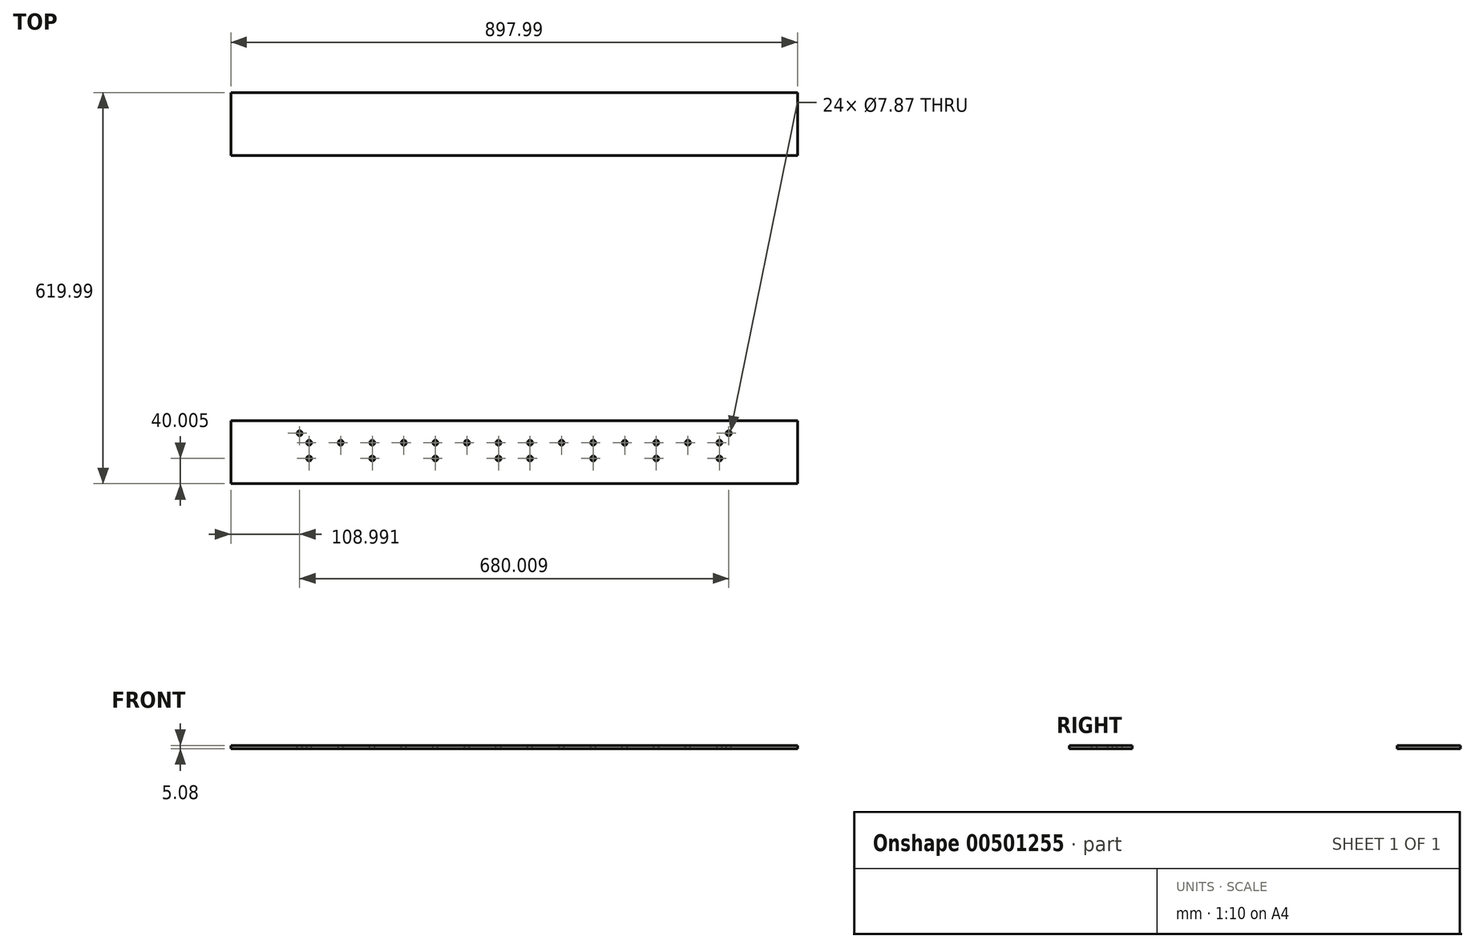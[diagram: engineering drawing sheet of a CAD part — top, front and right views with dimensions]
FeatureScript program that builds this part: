
annotation { "Feature Type Name" : "Feature", "Feature Type Description" : "" }
export const myFeature = defineFeature(function(context is Context, id is Id, definition is map)
    precondition{}
    {
        {
            var Q0;
            Q0=qCreatedBy(makeId("Top.planeOp"),FACE);
            var sketch = newSketch(context, id + "F0", { "sketchPlane" : qUnion([Q0])});
            skLineSegment(sketch, "E0.bottom", {"start": v(0, 0) * mm, "end": v(898, 0) * mm});
            skLineSegment(sketch, "E0.top", {"start": v(0, 100) * mm, "end": v(898, 100) * mm});
            skLineSegment(sketch, "E0.left", {"start": v(0, 0) * mm, "end": v(0, 100) * mm});
            skLineSegment(sketch, "E0.right", {"start": v(898, 0) * mm, "end": v(898, 100) * mm});
            skLineSegment(sketch, "E1.bottom", {"start": v(0, 100) * mm, "end": v(138.99, 100) * mm});
            skLineSegment(sketch, "E1.top", {"start": v(0, 519.99) * mm, "end": v(138.99, 519.99) * mm});
            skLineSegment(sketch, "E1.left", {"start": v(0, 100) * mm, "end": v(0, 519.99) * mm});
            skLineSegment(sketch, "E1.right", {"start": v(138.99, 100) * mm, "end": v(138.99, 519.99) * mm});
            skLineSegment(sketch, "E2.MirrorCS", {"start": v(898, 100) * mm, "end": v(759, 100) * mm});
            skLineSegment(sketch, "E3.MirrorCS", {"start": v(898, 100) * mm, "end": v(898, 519.99) * mm});
            skLineSegment(sketch, "E4.MirrorCS", {"start": v(898, 519.99) * mm, "end": v(759, 519.99) * mm});
            skLineSegment(sketch, "E5.MirrorCS", {"start": v(759, 100) * mm, "end": v(759, 519.99) * mm});
            skLineSegment(sketch, "E6.MirrorCS", {"start": v(0, 519.99) * mm, "end": v(898, 519.99) * mm});
            skLineSegment(sketch, "E7.MirrorCS", {"start": v(0, 619.99) * mm, "end": v(0, 519.99) * mm});
            skLineSegment(sketch, "E8.MirrorCS", {"start": v(0, 619.99) * mm, "end": v(898, 619.99) * mm});
            skLineSegment(sketch, "E9.MirrorCS", {"start": v(898, 619.99) * mm, "end": v(898, 519.99) * mm});
            skSolve(sketch);
        }
        {
            var Q0;
            Q0=makeQuery(id+"F0.imprint","IMPRINT",FACE,{"disambiguationData":[TD([[makeQuery(id+"F0.imprint","IMPRINT",EDGE,{"derivedFrom":sQuery(id+"F0.wireOp",EDGE,"E1.bottom")}),1.0]])]});
            var Q1;
            {var subQ0=sQuery(id+"F0.wireOp",EDGE,"E7.MirrorCS");Q1=makeQuery(id+"F0.imprint","IMPRINT",FACE,{"disambiguationData":[TD([[makeQuery(id+"F0.imprint","IMPRINT",EDGE,{"derivedFrom":subQ0}),1.0]])]});}
            var Q2;
            Q2=makeQuery(id+"F0.imprint","IMPRINT",FACE,{"disambiguationData":[TD([[makeQuery(id+"F0.imprint","IMPRINT",EDGE,{"derivedFrom":sQuery(id+"F0.wireOp",EDGE,"E2.MirrorCS")}),-1.0]])]});
            var Q3;
            Q3=makeQuery(id+"F0.imprint","IMPRINT",FACE,{"disambiguationData":[TD([[makeQuery(id+"F0.imprint","IMPRINT",EDGE,{"derivedFrom":sQuery(id+"F0.wireOp",EDGE,"E0.bottom")}),1.0]])]});
            extrude(context, id + "F1", {"entities" : qUnion([Q0, Q1, Q2, Q3]), "depth" : 5.08 * mm, "offsetDistance" : 25.4 * mm});
        }
        {
            var Q0;
            Q0=makeQuery(id+"F1.opExtrude","CAP_FACE",FACE,{"disambiguationData":[OSD([sQuery(id+"F0.wireOp",EDGE,"E0.bottom"),sQuery(id+"F0.wireOp",EDGE,"E0.top"),sQuery(id+"F0.wireOp",EDGE,"E0.left"),sQuery(id+"F0.wireOp",EDGE,"E0.right"),sQuery(id+"F0.wireOp",EDGE,"E1.left"),sQuery(id+"F0.wireOp",EDGE,"E1.right"),sQuery(id+"F0.wireOp",EDGE,"E3.MirrorCS"),sQuery(id+"F0.wireOp",EDGE,"E5.MirrorCS"),sQuery(id+"F0.wireOp",EDGE,"E6.MirrorCS"),sQuery(id+"F0.wireOp",EDGE,"E7.MirrorCS"),sQuery(id+"F0.wireOp",EDGE,"E8.MirrorCS"),sQuery(id+"F0.wireOp",EDGE,"E9.MirrorCS")])],"isStart":false});
            var sketch = newSketch(context, id + "F2", { "sketchPlane" : qUnion([Q0])});
            skLineSegment(sketch, "E10", {"start": v(0, 0) * mm, "end": v(124, 0) * mm});
            skLineSegment(sketch, "E11", {"start": v(124, 0) * mm, "end": v(124, 40) * mm});
            skLineSegment(sketch, "E12", {"start": v(124, 40) * mm, "end": v(124, 65) * mm});
            skCircle(sketch, "E13", {"center": v(124, 65) * mm, "radius": 3.94 * mm});
            skCircle(sketch, "E14.1.0.0", {"center": v(174.02, 65) * mm, "radius": 3.94 * mm});
            skCircle(sketch, "E14.2.0.0", {"center": v(224.03, 65) * mm, "radius": 3.94 * mm});
            skCircle(sketch, "E14.3.0.0", {"center": v(274.04, 65) * mm, "radius": 3.94 * mm});
            skCircle(sketch, "E14.4.0.0", {"center": v(324.05, 65) * mm, "radius": 3.94 * mm});
            skCircle(sketch, "E14.5.0.0", {"center": v(374.07, 65) * mm, "radius": 3.94 * mm});
            skCircle(sketch, "E14.6.0.0", {"center": v(424.08, 65) * mm, "radius": 3.94 * mm});
            skCircle(sketch, "E14.7.0.0", {"center": v(474.1, 65) * mm, "radius": 3.94 * mm});
            skCircle(sketch, "E14.8.0.0", {"center": v(524.1, 65) * mm, "radius": 3.94 * mm});
            skCircle(sketch, "E14.9.0.0", {"center": v(574.12, 65) * mm, "radius": 3.94 * mm});
            skCircle(sketch, "E14.10.0.0", {"center": v(624.13, 65) * mm, "radius": 3.94 * mm});
            skCircle(sketch, "E14.11.0.0", {"center": v(674.14, 65) * mm, "radius": 3.94 * mm});
            skCircle(sketch, "E14.12.0.0", {"center": v(724.15, 65) * mm, "radius": 3.94 * mm});
            skCircle(sketch, "E14.13.0.0", {"center": v(774.17, 65) * mm, "radius": 3.94 * mm});
            skLineSegment(sketch, "E14.direction1", {"start": v(124, 65) * mm, "end": v(174.02, 65) * mm, "construction": true});
            skLineSegment(sketch, "E15", {"start": v(138.99, 310) * mm, "end": v(268.02, 310) * mm});
            skPoint(sketch, "E15.endSnap0", {"position": v(138.99, 310) * mm});
            skCircle(sketch, "E16", {"center": v(124, 40) * mm, "radius": 3.94 * mm});
            skCircle(sketch, "E17.1.0.0", {"center": v(224.03, 40) * mm, "radius": 3.94 * mm});
            skCircle(sketch, "E17.2.0.0", {"center": v(324.05, 40) * mm, "radius": 3.94 * mm});
            skCircle(sketch, "E17.3.0.0", {"center": v(424.08, 40) * mm, "radius": 3.94 * mm});
            skLineSegment(sketch, "E17.direction1", {"start": v(124, 40) * mm, "end": v(224.03, 40) * mm, "construction": true});
            skLineSegment(sketch, "E18", {"start": v(424.08, 40) * mm, "end": v(474.1, 40) * mm});
            skCircle(sketch, "E19", {"center": v(474.1, 40) * mm, "radius": 3.94 * mm});
            skCircle(sketch, "E20.1.0.0", {"center": v(574.12, 40) * mm, "radius": 3.94 * mm});
            skCircle(sketch, "E20.2.0.0", {"center": v(674.14, 40) * mm, "radius": 3.94 * mm});
            skCircle(sketch, "E20.3.0.0", {"center": v(774.17, 40) * mm, "radius": 3.94 * mm});
            skLineSegment(sketch, "E20.direction1", {"start": v(474.1, 40) * mm, "end": v(574.12, 40) * mm, "construction": true});
            skCircle(sketch, "E21.MirrorC", {"center": v(124, 579.98) * mm, "radius": 3.94 * mm});
            skCircle(sketch, "E22.MirrorC", {"center": v(124, 555) * mm, "radius": 3.94 * mm});
            skCircle(sketch, "E23.MirrorC", {"center": v(174.02, 555) * mm, "radius": 3.94 * mm});
            skCircle(sketch, "E24.MirrorC", {"center": v(224.03, 555) * mm, "radius": 3.94 * mm});
            skCircle(sketch, "E25.MirrorC", {"center": v(224.03, 579.98) * mm, "radius": 3.94 * mm});
            skCircle(sketch, "E26.MirrorC", {"center": v(274.04, 555) * mm, "radius": 3.94 * mm});
            skCircle(sketch, "E27.MirrorC", {"center": v(324.05, 555) * mm, "radius": 3.94 * mm});
            skCircle(sketch, "E28.MirrorC", {"center": v(324.05, 579.98) * mm, "radius": 3.94 * mm});
            skCircle(sketch, "E29.MirrorC", {"center": v(374.07, 555) * mm, "radius": 3.94 * mm});
            skCircle(sketch, "E30.MirrorC", {"center": v(424.08, 555) * mm, "radius": 3.94 * mm});
            skCircle(sketch, "E31.MirrorC", {"center": v(424.08, 579.98) * mm, "radius": 3.94 * mm});
            skCircle(sketch, "E32.MirrorC", {"center": v(474.1, 555) * mm, "radius": 3.94 * mm});
            skCircle(sketch, "E33.MirrorC", {"center": v(474.1, 579.98) * mm, "radius": 3.94 * mm});
            skCircle(sketch, "E34.MirrorC", {"center": v(524.1, 555) * mm, "radius": 3.94 * mm});
            skCircle(sketch, "E35.MirrorC", {"center": v(624.13, 555) * mm, "radius": 3.94 * mm});
            skCircle(sketch, "E36.MirrorC", {"center": v(674.14, 555) * mm, "radius": 3.94 * mm});
            skCircle(sketch, "E37.MirrorC", {"center": v(674.14, 579.98) * mm, "radius": 3.94 * mm});
            skCircle(sketch, "E38.MirrorC", {"center": v(724.15, 555) * mm, "radius": 3.94 * mm});
            skCircle(sketch, "E39.MirrorC", {"center": v(774.17, 555) * mm, "radius": 3.94 * mm});
            skCircle(sketch, "E40.MirrorC", {"center": v(774.17, 579.98) * mm, "radius": 3.94 * mm});
            skCircle(sketch, "E41.MirrorC", {"center": v(574.12, 555) * mm, "radius": 3.94 * mm});
            skCircle(sketch, "E42.MirrorC", {"center": v(574.12, 579.98) * mm, "radius": 3.94 * mm});
            skLineSegment(sketch, "E43", {"start": v(124, 65) * mm, "end": v(109, 65) * mm});
            skLineSegment(sketch, "E44", {"start": v(109, 65) * mm, "end": v(109, 80) * mm});
            skCircle(sketch, "E45", {"center": v(109, 80) * mm, "radius": 3.94 * mm});
            skLineSegment(sketch, "E46", {"start": v(449, 100) * mm, "end": v(449, 150.02) * mm});
            skCircle(sketch, "E47.MirrorC", {"center": v(789, 80) * mm, "radius": 3.94 * mm});
            skCircle(sketch, "E48.MirrorC", {"center": v(109, 539.98) * mm, "radius": 3.94 * mm});
            skCircle(sketch, "E49.MirrorC", {"center": v(789, 539.98) * mm, "radius": 3.94 * mm});
            skCircle(sketch, "E50.0.1.0", {"center": v(109, 130.02) * mm, "radius": 3.94 * mm});
            skCircle(sketch, "E50.0.2.0", {"center": v(109, 180.04) * mm, "radius": 3.94 * mm});
            skCircle(sketch, "E50.0.3.0", {"center": v(109, 230.05) * mm, "radius": 3.94 * mm});
            skCircle(sketch, "E50.0.4.0", {"center": v(109, 280.06) * mm, "radius": 3.94 * mm});
            skCircle(sketch, "E50.0.5.0", {"center": v(109, 330.07) * mm, "radius": 3.94 * mm});
            skCircle(sketch, "E50.0.6.0", {"center": v(109, 380.09) * mm, "radius": 3.94 * mm});
            skCircle(sketch, "E50.0.7.0", {"center": v(109, 430.1) * mm, "radius": 3.94 * mm});
            skCircle(sketch, "E50.0.8.0", {"center": v(109, 480.11) * mm, "radius": 3.94 * mm});
            skLineSegment(sketch, "E50.direction1", {"start": v(109, 80) * mm, "end": v(134.4, 80) * mm, "construction": true});
            skLineSegment(sketch, "E50.direction2", {"start": v(109, 80) * mm, "end": v(109, 130.02) * mm, "construction": true});
            skLineSegment(sketch, "E51", {"start": v(109, 130.02) * mm, "end": v(84, 130.02) * mm});
            skLineSegment(sketch, "E52", {"start": v(84, 130.02) * mm, "end": v(84, 145.03) * mm});
            skCircle(sketch, "E53", {"center": v(84, 145.03) * mm, "radius": 3.94 * mm});
            skCircle(sketch, "E54.0.1.0", {"center": v(84, 225.04) * mm, "radius": 3.94 * mm});
            skCircle(sketch, "E54.0.2.0", {"center": v(84, 305.05) * mm, "radius": 3.94 * mm});
            skCircle(sketch, "E54.0.3.0", {"center": v(84, 385.06) * mm, "radius": 3.94 * mm});
            skCircle(sketch, "E54.0.4.0", {"center": v(84, 465.07) * mm, "radius": 3.94 * mm});
            skLineSegment(sketch, "E54.direction1", {"start": v(84, 145.03) * mm, "end": v(109.4, 145.03) * mm, "construction": true});
            skLineSegment(sketch, "E54.direction2", {"start": v(84, 145.03) * mm, "end": v(84, 225.04) * mm, "construction": true});
            skCircle(sketch, "E55.MirrorC", {"center": v(789, 480.11) * mm, "radius": 3.94 * mm});
            skCircle(sketch, "E56.MirrorC", {"center": v(814, 465.07) * mm, "radius": 3.94 * mm});
            skCircle(sketch, "E57.MirrorC", {"center": v(789, 430.1) * mm, "radius": 3.94 * mm});
            skCircle(sketch, "E58.MirrorC", {"center": v(814, 385.06) * mm, "radius": 3.94 * mm});
            skCircle(sketch, "E59.MirrorC", {"center": v(789, 380.09) * mm, "radius": 3.94 * mm});
            skCircle(sketch, "E60.MirrorC", {"center": v(789, 330.07) * mm, "radius": 3.94 * mm});
            skCircle(sketch, "E61.MirrorC", {"center": v(814, 305.05) * mm, "radius": 3.94 * mm});
            skCircle(sketch, "E62.MirrorC", {"center": v(789, 280.06) * mm, "radius": 3.94 * mm});
            skCircle(sketch, "E63.MirrorC", {"center": v(789, 130.02) * mm, "radius": 3.94 * mm});
            skCircle(sketch, "E64.MirrorC", {"center": v(814, 145.03) * mm, "radius": 3.94 * mm});
            skCircle(sketch, "E65.MirrorC", {"center": v(789, 180.04) * mm, "radius": 3.94 * mm});
            skCircle(sketch, "E66.MirrorC", {"center": v(814, 225.04) * mm, "radius": 3.94 * mm});
            skCircle(sketch, "E67.MirrorC", {"center": v(789, 230.05) * mm, "radius": 3.94 * mm});
            skSolve(sketch);
        }
        {
            var Q0;
            Q0=sQuery(id+"F2.wireOp",VERTEX,"E48.MirrorC.center");
            var Q1;
            Q1=sQuery(id+"F2.wireOp",VERTEX,"E22.MirrorC.center");
            var Q2;
            Q2=sQuery(id+"F2.wireOp",VERTEX,"E23.MirrorC.center");
            var Q3;
            Q3=sQuery(id+"F2.wireOp",VERTEX,"E21.MirrorC.center");
            var Q4;
            Q4=sQuery(id+"F2.wireOp",VERTEX,"E25.MirrorC.center");
            var Q5;
            Q5=sQuery(id+"F2.wireOp",VERTEX,"E24.MirrorC.center");
            var Q6;
            Q6=sQuery(id+"F2.wireOp",VERTEX,"E26.MirrorC.center");
            var Q7;
            Q7=sQuery(id+"F2.wireOp",VERTEX,"E28.MirrorC.center");
            var Q8;
            Q8=sQuery(id+"F2.wireOp",VERTEX,"E27.MirrorC.center");
            var Q9;
            Q9=sQuery(id+"F2.wireOp",VERTEX,"E29.MirrorC.center");
            var Q10;
            Q10=sQuery(id+"F2.wireOp",VERTEX,"E31.MirrorC.center");
            var Q11;
            Q11=sQuery(id+"F2.wireOp",VERTEX,"E30.MirrorC.center");
            var Q12;
            Q12=sQuery(id+"F2.wireOp",VERTEX,"E33.MirrorC.center");
            var Q13;
            Q13=sQuery(id+"F2.wireOp",VERTEX,"E32.MirrorC.center");
            var Q14;
            Q14=sQuery(id+"F2.wireOp",VERTEX,"E34.MirrorC.center");
            var Q15;
            Q15=sQuery(id+"F2.wireOp",VERTEX,"E42.MirrorC.center");
            var Q16;
            Q16=sQuery(id+"F2.wireOp",VERTEX,"E41.MirrorC.center");
            var Q17;
            Q17=sQuery(id+"F2.wireOp",VERTEX,"E35.MirrorC.center");
            var Q18;
            Q18=sQuery(id+"F2.wireOp",VERTEX,"E37.MirrorC.center");
            var Q19;
            Q19=sQuery(id+"F2.wireOp",VERTEX,"E36.MirrorC.center");
            var Q20;
            Q20=sQuery(id+"F2.wireOp",VERTEX,"E49.MirrorC.center");
            var Q21;
            Q21=sQuery(id+"F2.wireOp",VERTEX,"E40.MirrorC.center");
            var Q22;
            Q22=sQuery(id+"F2.wireOp",VERTEX,"E39.MirrorC.center");
            var Q23;
            Q23=sQuery(id+"F2.wireOp",VERTEX,"E38.MirrorC.center");
            var Q24;
            Q24=sQuery(id+"F2.wireOp",VERTEX,"E55.MirrorC.center");
            var Q25;
            Q25=sQuery(id+"F2.wireOp",VERTEX,"E56.MirrorC.center");
            var Q26;
            Q26=sQuery(id+"F2.wireOp",VERTEX,"E63.MirrorC.center");
            var Q27;
            Q27=sQuery(id+"F2.wireOp",VERTEX,"E64.MirrorC.center");
            var Q28;
            Q28=sQuery(id+"F2.wireOp",VERTEX,"E65.MirrorC.center");
            var Q29;
            Q29=sQuery(id+"F2.wireOp",VERTEX,"E67.MirrorC.center");
            var Q30;
            Q30=sQuery(id+"F2.wireOp",VERTEX,"E66.MirrorC.center");
            var Q31;
            Q31=sQuery(id+"F2.wireOp",VERTEX,"E62.MirrorC.center");
            var Q32;
            Q32=sQuery(id+"F2.wireOp",VERTEX,"E61.MirrorC.center");
            var Q33;
            Q33=sQuery(id+"F2.wireOp",VERTEX,"E60.MirrorC.center");
            var Q34;
            Q34=sQuery(id+"F2.wireOp",VERTEX,"E59.MirrorC.center");
            var Q35;
            Q35=sQuery(id+"F2.wireOp",VERTEX,"E58.MirrorC.center");
            var Q36;
            Q36=sQuery(id+"F2.wireOp",VERTEX,"E57.MirrorC.center");
            var Q37;
            Q37=sQuery(id+"F2.wireOp",VERTEX,"E47.MirrorC.center");
            var Q38;
            Q38=sQuery(id+"F2.wireOp",VERTEX,"E14.13.0.0.center");
            var Q39;
            Q39=sQuery(id+"F2.wireOp",VERTEX,"E20.3.0.0.center");
            var Q40;
            Q40=sQuery(id+"F2.wireOp",VERTEX,"E14.12.0.0.center");
            var Q41;
            Q41=sQuery(id+"F2.wireOp",VERTEX,"E14.11.0.0.center");
            var Q42;
            Q42=sQuery(id+"F2.wireOp",VERTEX,"E20.2.0.0.center");
            var Q43;
            Q43=sQuery(id+"F2.wireOp",VERTEX,"E54.0.4.0.center");
            var Q44;
            Q44=sQuery(id+"F2.wireOp",VERTEX,"E50.0.8.0.center");
            var Q45;
            Q45=sQuery(id+"F2.wireOp",VERTEX,"E50.0.7.0.center");
            var Q46;
            Q46=sQuery(id+"F2.wireOp",VERTEX,"E54.0.3.0.center");
            var Q47;
            Q47=sQuery(id+"F2.wireOp",VERTEX,"E50.0.6.0.center");
            var Q48;
            Q48=sQuery(id+"F2.wireOp",VERTEX,"E50.0.5.0.center");
            var Q49;
            Q49=sQuery(id+"F2.wireOp",VERTEX,"E54.0.2.0.center");
            var Q50;
            Q50=sQuery(id+"F2.wireOp",VERTEX,"E50.0.4.0.center");
            var Q51;
            Q51=sQuery(id+"F2.wireOp",VERTEX,"E54.direction2.end");
            var Q52;
            Q52=sQuery(id+"F2.wireOp",VERTEX,"E50.0.3.0.center");
            var Q53;
            Q53=sQuery(id+"F2.wireOp",VERTEX,"E50.0.2.0.center");
            var Q54;
            Q54=sQuery(id+"F2.wireOp",VERTEX,"E53.center");
            var Q55;
            Q55=sQuery(id+"F2.wireOp",VERTEX,"E51.start");
            var Q56;
            Q56=sQuery(id+"F2.wireOp",VERTEX,"E50.direction2.start");
            var Q57;
            Q57=sQuery(id+"F2.wireOp",VERTEX,"E14.direction1.start");
            var Q58;
            Q58=sQuery(id+"F2.wireOp",VERTEX,"E17.direction1.start");
            var Q59;
            Q59=sQuery(id+"F2.wireOp",VERTEX,"E14.direction1.end");
            var Q60;
            Q60=sQuery(id+"F2.wireOp",VERTEX,"E17.direction1.end");
            var Q61;
            Q61=sQuery(id+"F2.wireOp",VERTEX,"E14.2.0.0.center");
            var Q62;
            Q62=sQuery(id+"F2.wireOp",VERTEX,"E14.3.0.0.center");
            var Q63;
            Q63=sQuery(id+"F2.wireOp",VERTEX,"E17.2.0.0.center");
            var Q64;
            Q64=sQuery(id+"F2.wireOp",VERTEX,"E14.4.0.0.center");
            var Q65;
            Q65=sQuery(id+"F2.wireOp",VERTEX,"E14.5.0.0.center");
            var Q66;
            Q66=sQuery(id+"F2.wireOp",VERTEX,"E14.6.0.0.center");
            var Q67;
            Q67=sQuery(id+"F2.wireOp",VERTEX,"E18.start");
            var Q68;
            Q68=sQuery(id+"F2.wireOp",VERTEX,"E14.7.0.0.center");
            var Q69;
            Q69=sQuery(id+"F2.wireOp",VERTEX,"E20.direction1.start");
            var Q70;
            Q70=sQuery(id+"F2.wireOp",VERTEX,"E14.8.0.0.center");
            var Q71;
            Q71=sQuery(id+"F2.wireOp",VERTEX,"E14.9.0.0.center");
            var Q72;
            Q72=sQuery(id+"F2.wireOp",VERTEX,"E14.10.0.0.center");
            var Q73;
            Q73=sQuery(id+"F2.wireOp",VERTEX,"E20.direction1.end");
            var Q74;
            Q74=makeQuery(id+"F1.opExtrude","SWEPT_BODY",BODY,{"disambiguationData":[OSD([sQuery(id+"F0.wireOp",EDGE,"E0.bottom"),sQuery(id+"F0.wireOp",EDGE,"E0.top"),sQuery(id+"F0.wireOp",EDGE,"E0.left"),sQuery(id+"F0.wireOp",EDGE,"E0.right"),sQuery(id+"F0.wireOp",EDGE,"E1.left"),sQuery(id+"F0.wireOp",EDGE,"E1.right"),sQuery(id+"F0.wireOp",EDGE,"E3.MirrorCS"),sQuery(id+"F0.wireOp",EDGE,"E5.MirrorCS"),sQuery(id+"F0.wireOp",EDGE,"E6.MirrorCS"),sQuery(id+"F0.wireOp",EDGE,"E7.MirrorCS"),sQuery(id+"F0.wireOp",EDGE,"E8.MirrorCS"),sQuery(id+"F0.wireOp",EDGE,"E9.MirrorCS")])]});
            hole(context, id + "F3", {"style" : HoleStyle.SIMPLE, "endStyle" : HoleEndStyle.THROUGH, "holeDiameter" : 7.87 * mm, "isTappedThrough" : true, "tappedDepth" : 12.7 * mm, "tapClearance" : 3, "locations" : qUnion([Q0, Q1, Q2, Q3, Q4, Q5, Q6, Q7, Q8, Q9, Q10, Q11, Q12, Q13, Q14, Q15, Q16, Q17, Q18, Q19, Q20, Q21, Q22, Q23, Q24, Q25, Q26, Q27, Q28, Q29, Q30, Q31, Q32, Q33, Q34, Q35, Q36, Q37, Q38, Q39, Q40, Q41, Q42, Q43, Q44, Q45, Q46, Q47, Q48, Q49, Q50, Q51, Q52, Q53, Q54, Q55, Q56, Q57, Q58, Q59, Q60, Q61, Q62, Q63, Q64, Q65, Q66, Q67, Q68, Q69, Q70, Q71, Q72, Q73]), "scope" : qUnion([Q74])});
        }
    });
